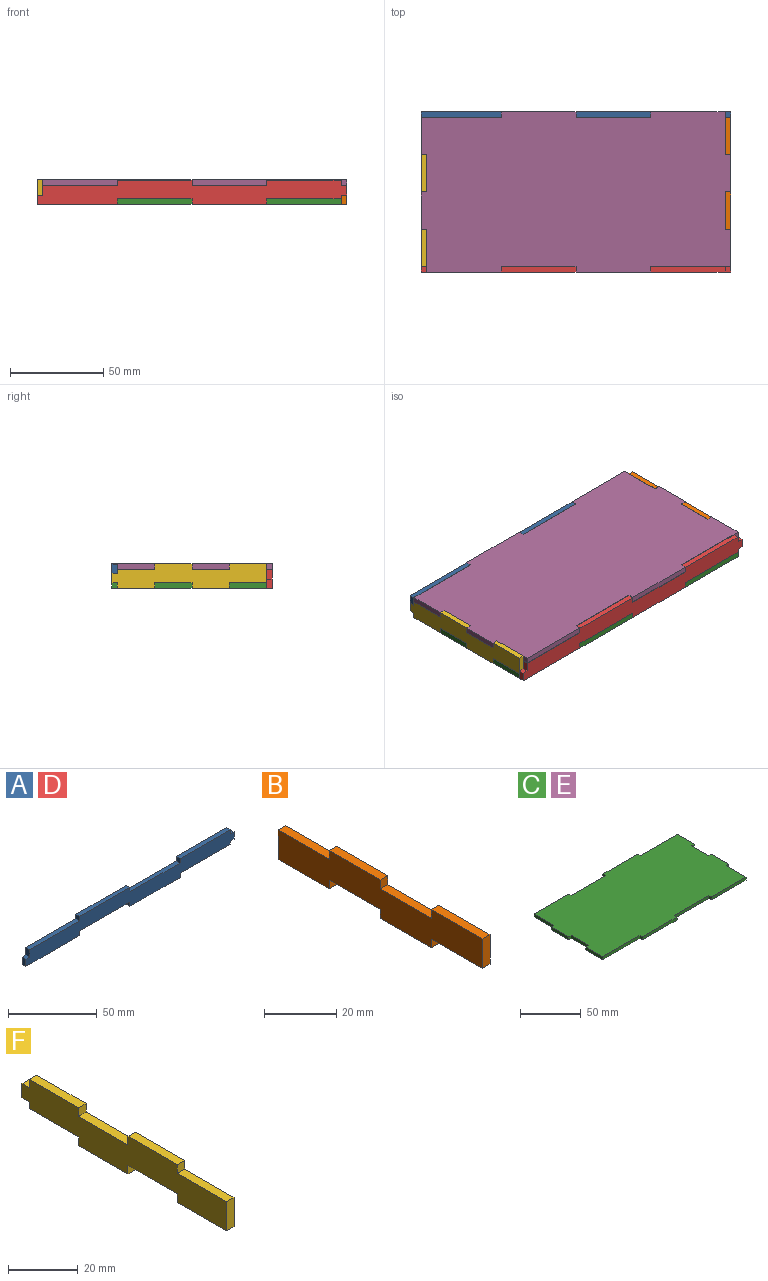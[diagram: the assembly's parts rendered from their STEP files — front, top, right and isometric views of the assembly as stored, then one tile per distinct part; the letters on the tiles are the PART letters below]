
ASSEMBLY  parts=6 mates=4
PART A: 24 faces, bbox 166x3x13 mm
  f0: plane 40x3mm, normal (0,0,-1), area 120mm2, adj f1,f21,f22,f23
  f1: plane 3x3mm, normal (1,0,0), area 9mm2, adj f0,f2,f22,f23
  f2: plane 40x3mm, normal (0,0,-1), area 120mm2, adj f1,f3,f22,f23
  f3: plane 3x2mm, normal (1,0,0), area 6mm2, adj f2,f4,f22,f23
  f4: plane 3x3mm, normal (0,0,-1), area 9mm2, adj f3,f5,f22,f23
  f5: plane 5x3mm, normal (1,0,0), area 15mm2, adj f4,f6,f22,f23
  f6: plane 3x3mm, normal (0,0,1), area 9mm2, adj f5,f7,f22,f23
  f7: plane 3x3mm, normal (1,0,0), area 9mm2, adj f6,f8,f22,f23
  f8: plane 40x3mm, normal (0,0,1), area 120mm2, adj f7,f9,f22,f23
  f9: plane 3x3mm, normal (-1,0,0), area 9mm2, adj f8,f10,f22,f23
  f10: plane 40x3mm, normal (0,0,1), area 120mm2, adj f9,f11,f22,f23
  f11: plane 3x3mm, normal (1,0,0), area 9mm2, adj f10,f12,f22,f23
  f12: plane 40x3mm, normal (0,0,1), area 120mm2, adj f11,f13,f22,f23
  f13: plane 3x3mm, normal (-1,0,0), area 9mm2, adj f12,f14,f22,f23
  f14: plane 40x3mm, normal (0,0,1), area 120mm2, adj f13,f15,f22,f23
  f15: plane 5x3mm, normal (-1,0,0), area 15mm2, adj f14,f16,f22,f23
  f16: plane 3x3mm, normal (0,0,1), area 9mm2, adj f15,f17,f22,f23
  f17: plane 5x3mm, normal (-1,0,0), area 15mm2, adj f16,f18,f22,f23
  f18: plane 43x3mm, normal (0,0,-1), area 129mm2, adj f17,f19,f22,f23
  f19: plane 3x3mm, normal (1,0,0), area 9mm2, adj f18,f20,f22,f23
  f20: plane 40x3mm, normal (0,0,-1), area 120mm2, adj f19,f21,f22,f23
  f21: plane 3x3mm, normal (-1,0,0), area 9mm2, adj f0,f20,f22,f23
  f22: plane 166x13mm, normal (0,1,0), area 1630mm2, adj f0,f1,f2,f3,f4,f5,f6,f7
  f23: plane 166x13mm, normal (0,-1,0), area 1630mm2, adj f0,f1,f2,f3,f4,f5,f6,f7
PART B: 18 faces, bbox 3x80x13 mm
  f0: plane 20x3mm, normal (0,0,-1), area 60mm2, adj f1,f15,f16,f17
  f1: plane 3x3mm, normal (0,-1,0), area 9mm2, adj f0,f2,f16,f17
  f2: plane 20x3mm, normal (0,0,-1), area 60mm2, adj f1,f3,f16,f17
  f3: plane 10x3mm, normal (0,-1,0), area 30mm2, adj f2,f4,f16,f17
  f4: plane 20x3mm, normal (0,0,1), area 60mm2, adj f3,f5,f16,f17
  f5: plane 3x3mm, normal (0,1,0), area 9mm2, adj f4,f6,f16,f17
  f6: plane 20x3mm, normal (0,0,1), area 60mm2, adj f5,f7,f16,f17
  f7: plane 3x3mm, normal (0,-1,0), area 9mm2, adj f6,f8,f16,f17
  f8: plane 20x3mm, normal (0,0,1), area 60mm2, adj f7,f9,f16,f17
  f9: plane 3x3mm, normal (0,1,0), area 9mm2, adj f8,f10,f16,f17
  f10: plane 20x3mm, normal (0,0,1), area 60mm2, adj f9,f11,f16,f17
  f11: plane 10x3mm, normal (0,1,0), area 30mm2, adj f10,f12,f16,f17
  f12: plane 20x3mm, normal (0,0,-1), area 60mm2, adj f11,f13,f16,f17
  f13: plane 3x3mm, normal (0,-1,0), area 9mm2, adj f12,f14,f16,f17
  f14: plane 20x3mm, normal (0,0,-1), area 60mm2, adj f13,f15,f16,f17
  f15: plane 3x3mm, normal (0,1,0), area 9mm2, adj f0,f14,f16,f17
  f16: plane 80x13mm, normal (1,0,0), area 800mm2, adj f0,f1,f2,f3,f4,f5,f6,f7
  f17: plane 80x13mm, normal (-1,0,0), area 800mm2, adj f0,f1,f2,f3,f4,f5,f6,f7
PART C: 30 faces, bbox 166x86x3 mm
  f0: plane 40x3mm, normal (0,1,0), area 120mm2, adj f1,f27,f28,f29
  f1: plane 3x3mm, normal (-1,0,0), area 9mm2, adj f0,f2,f28,f29
  f2: plane 40x3mm, normal (0,1,0), area 120mm2, adj f1,f3,f28,f29
  f3: plane 3x3mm, normal (1,0,0), area 9mm2, adj f2,f4,f28,f29
  f4: plane 40x3mm, normal (0,1,0), area 120mm2, adj f3,f5,f28,f29
  f5: plane 23x3mm, normal (-1,0,0), area 69mm2, adj f4,f6,f28,f29
  f6: plane 3x3mm, normal (0,1,0), area 9mm2, adj f5,f7,f28,f29
  f7: plane 20x3mm, normal (-1,0,0), area 60mm2, adj f6,f8,f28,f29
  f8: plane 3x3mm, normal (0,-1,0), area 9mm2, adj f7,f9,f28,f29
  f9: plane 20x3mm, normal (-1,0,0), area 60mm2, adj f8,f10,f28,f29
  f10: plane 3x3mm, normal (0,1,0), area 9mm2, adj f9,f11,f28,f29
  f11: plane 20x3mm, normal (-1,0,0), area 60mm2, adj f10,f12,f28,f29
  f12: plane 43x3mm, normal (0,-1,0), area 129mm2, adj f11,f13,f28,f29
  f13: plane 3x3mm, normal (-1,0,0), area 9mm2, adj f12,f14,f28,f29
  f14: plane 40x3mm, normal (0,-1,0), area 120mm2, adj f13,f15,f28,f29
  f15: plane 3x3mm, normal (1,0,0), area 9mm2, adj f14,f16,f28,f29
  f16: plane 40x3mm, normal (0,-1,0), area 120mm2, adj f15,f17,f28,f29
  f17: plane 3x3mm, normal (-1,0,0), area 9mm2, adj f16,f18,f28,f29
  f18: plane 40x3mm, normal (0,-1,0), area 120mm2, adj f17,f19,f28,f29
  f19: plane 23x3mm, normal (1,0,0), area 69mm2, adj f18,f20,f28,f29
  f20: plane 3x3mm, normal (0,-1,0), area 9mm2, adj f19,f21,f28,f29
  f21: plane 20x3mm, normal (1,0,0), area 60mm2, adj f20,f22,f28,f29
  f22: plane 3x3mm, normal (0,1,0), area 9mm2, adj f21,f23,f28,f29
  f23: plane 20x3mm, normal (1,0,0), area 60mm2, adj f22,f24,f28,f29
  f24: plane 3x3mm, normal (0,-1,0), area 9mm2, adj f23,f25,f28,f29
  f25: plane 20x3mm, normal (1,0,0), area 60mm2, adj f24,f26,f28,f29
  f26: plane 43x3mm, normal (0,1,0), area 129mm2, adj f25,f27,f28,f29
  f27: plane 3x3mm, normal (1,0,0), area 9mm2, adj f0,f26,f28,f29
  f28: plane 166x86mm, normal (0,0,1), area 13520mm2, adj f0,f1,f2,f3,f4,f5,f6,f7
  f29: plane 166x86mm, normal (0,0,-1), area 13520mm2, adj f0,f1,f2,f3,f4,f5,f6,f7
PART D: same geometry as A
PART E: same geometry as C
PART F: 22 faces, bbox 3x83x13.2 mm
  f0: plane 20x3mm, normal (0,0,-1), area 60mm2, adj f1,f19,f20,f21
  f1: plane 3x2.23mm, normal (0,1,0), area 6.7mm2, adj f0,f2,f20,f21
  f2: plane 3x3mm, normal (0,0,-1), area 9mm2, adj f1,f3,f20,f21
  f3: plane 5x3mm, normal (0,1,0), area 15mm2, adj f2,f4,f20,f21
  f4: plane 3x3mm, normal (0,0,1), area 9mm2, adj f3,f5,f20,f21
  f5: plane 3x3mm, normal (0,1,0), area 9mm2, adj f4,f6,f20,f21
  f6: plane 20x3mm, normal (0,0,1), area 60mm2, adj f5,f7,f20,f21
  f7: plane 3x3mm, normal (0,-1,0), area 9mm2, adj f6,f8,f20,f21
  f8: plane 20x3mm, normal (0,0,1), area 60mm2, adj f7,f9,f20,f21
  f9: plane 3x3mm, normal (0,1,0), area 9mm2, adj f8,f10,f20,f21
  f10: plane 20x3mm, normal (0,0,1), area 60mm2, adj f9,f11,f20,f21
  f11: plane 3x3mm, normal (0,-1,0), area 9mm2, adj f10,f12,f20,f21
  f12: plane 20x3mm, normal (0,0,1), area 60mm2, adj f11,f13,f20,f21
  f13: plane 10.23x3mm, normal (0,-1,0), area 30.7mm2, adj f12,f14,f20,f21
  f14: plane 20x3mm, normal (0,0,-1), area 60mm2, adj f13,f15,f20,f21
  f15: plane 3x3mm, normal (0,1,0), area 9mm2, adj f14,f16,f20,f21
  f16: plane 20x3mm, normal (0,0,-1), area 60mm2, adj f15,f17,f20,f21
  f17: plane 3x3mm, normal (0,-1,0), area 9mm2, adj f16,f18,f20,f21
  f18: plane 20x3mm, normal (0,0,-1), area 60mm2, adj f17,f19,f20,f21
  f19: plane 3x3mm, normal (0,1,0), area 9mm2, adj f0,f18,f20,f21
  f20: plane 83x13.23mm, normal (-1,0,0), area 833.2mm2, adj f0,f1,f2,f3,f4,f5,f6,f7
  f21: plane 83x13.23mm, normal (1,0,0), area 833.2mm2, adj f0,f1,f2,f3,f4,f5,f6,f7
PLACE A rot(axis=(-1,0,0),180deg) t=(1.27,5.07,33.62)mm
PLACE B rot(axis=(0,-1,0),180deg) t=(1.27,5.07,33.62)mm
PLACE C t=(1.27,5.07,20.62)mm
PLACE D t=(1.27,5.07,20.62)mm
PLACE E rot(axis=(1,0,0),180deg) t=(1.27,5.07,33.85)mm
PLACE F rot(axis=(0,1,0),180deg) t=(1.27,5.07,33.85)mm
MATE fastened A.f11 <-> C.f1  axis (1,0,0) through (1.27,46.57,22.12)mm
MATE fastened B.f9 <-> C.f24  axis (0,1,0) through (82.77,25.07,22.12)mm
MATE fastened F.f19 <-> E.f10  axis (0,1,0) through (-80.23,25.07,32.35)mm
MATE fastened D.f21 <-> C.f15  axis (-1,0,0) through (1.27,-36.43,22.12)mm
